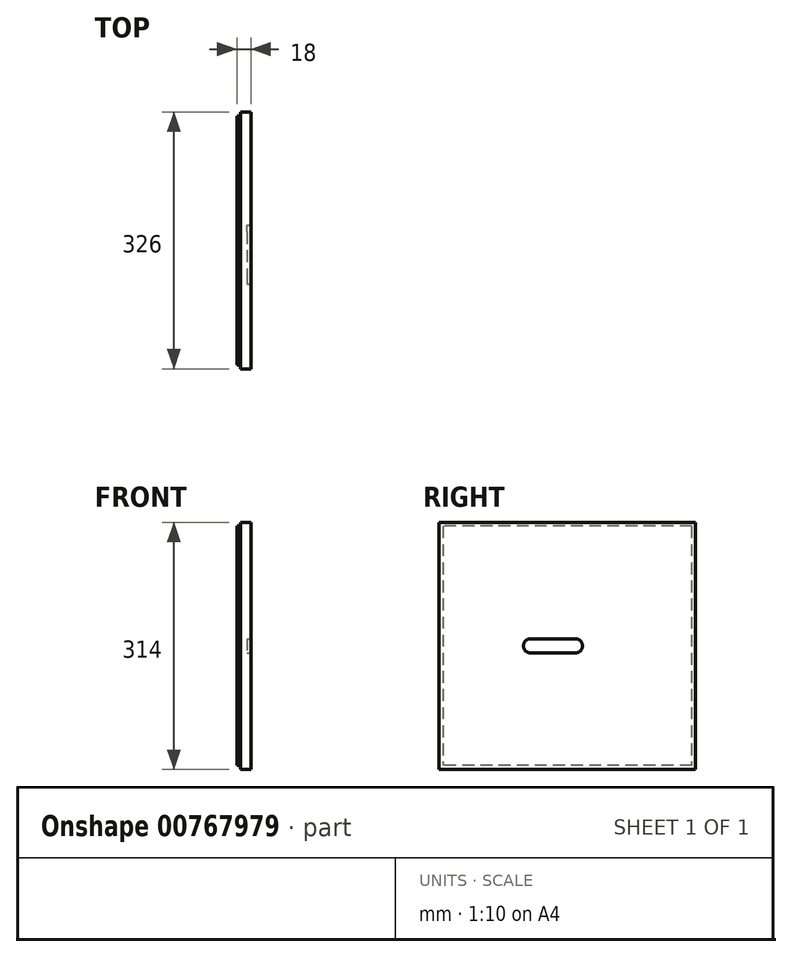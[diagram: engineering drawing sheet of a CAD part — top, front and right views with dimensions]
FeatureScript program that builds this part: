
annotation { "Feature Type Name" : "Feature", "Feature Type Description" : "" }
export const myFeature = defineFeature(function(context is Context, id is Id, definition is map)
    precondition{}
    {
        {
            var Q0;
            Q0=qCreatedBy(makeId("Right.planeOp"),FACE);
            var sketch = newSketch(context, id + "F0", { "sketchPlane" : qUnion([Q0])});
            skLineSegment(sketch, "E0.bottom", {"start": v(-163, 157) * mm, "end": v(163, 157) * mm});
            skLineSegment(sketch, "E0.top", {"start": v(-163, -157) * mm, "end": v(163, -157) * mm});
            skLineSegment(sketch, "E0.left", {"start": v(-163, 157) * mm, "end": v(-163, -157) * mm});
            skLineSegment(sketch, "E0.right", {"start": v(163, 157) * mm, "end": v(163, -157) * mm});
            skPoint(sketch, "E0.middle", {"position": v(0, 0) * mm});
            skSolve(sketch);
        }
        {
            var Q0;
            Q0 = qSketchRegion(id + "F0", true);
            extrude(context, id + "F1", {"entities" : qUnion([Q0]), "oppositeDirection" : true, "depth" : 18 * mm, "offsetDistance" : 25 * mm});
        }
        {
            var Q0;
            Q0=makeQuery(id+"F1.opExtrude","CAP_FACE",FACE,{"disambiguationData":[OSD([sQuery(id+"F0.wireOp",EDGE,"E0.bottom"),sQuery(id+"F0.wireOp",EDGE,"E0.top"),sQuery(id+"F0.wireOp",EDGE,"E0.left"),sQuery(id+"F0.wireOp",EDGE,"E0.right")])],"isStart":true});
            var sketch = newSketch(context, id + "F2", { "sketchPlane" : qUnion([Q0])});
            skLineSegment(sketch, "E1", {"start": v(-163, 0) * mm, "end": v(-18, 0) * mm, "construction": true});
            skLineSegment(sketch, "E2.bottom", {"start": v(10.5, 9) * mm, "end": v(-46.5, 9) * mm});
            skLineSegment(sketch, "E2.top", {"start": v(10.5, -9) * mm, "end": v(-46.5, -9) * mm});
            skLineSegment(sketch, "E2.left", {"start": v(10.5, 9) * mm, "end": v(10.5, -9) * mm, "construction": true});
            skLineSegment(sketch, "E2.right", {"start": v(-46.5, 9) * mm, "end": v(-46.5, -9) * mm, "construction": true});
            skPoint(sketch, "E2.middle", {"position": v(-18, 0) * mm});
            skArc(sketch, "E3", {"start": v(-46.5, 9) * mm, "mid": v(-55.5, 0) * mm, "end": v(-46.5, -9) * mm});
            skArc(sketch, "E4", {"start": v(10.5, 9) * mm, "mid": v(19.5, 0) * mm, "end": v(10.5, -9) * mm});
            skSolve(sketch);
        }
        {
            var Q0;
            Q0 = qSketchRegion(id + "F2", true);
            extrude(context, id + "F3", {"entities" : qUnion([Q0]), "operationType" : NewBodyOperationType.REMOVE, "oppositeDirection" : true, "depth" : 5 * mm, "offsetDistance" : 25 * mm});
        }
        {
            var Q0;
            Q0=makeQuery(id+"F1.opExtrude","CAP_FACE",FACE,{"disambiguationData":[OSD([sQuery(id+"F0.wireOp",EDGE,"E0.bottom"),sQuery(id+"F0.wireOp",EDGE,"E0.top"),sQuery(id+"F0.wireOp",EDGE,"E0.left"),sQuery(id+"F0.wireOp",EDGE,"E0.right")])],"isStart":false});
            var sketch = newSketch(context, id + "F4", { "sketchPlane" : qUnion([Q0])});
            skLineSegment(sketch, "E5.bottom", {"start": v(-163, 157) * mm, "end": v(163, 157) * mm});
            skLineSegment(sketch, "E5.top", {"start": v(-163, -157) * mm, "end": v(163, -157) * mm});
            skLineSegment(sketch, "E5.left", {"start": v(-163, 157) * mm, "end": v(-163, -157) * mm});
            skLineSegment(sketch, "E5.right", {"start": v(163, 157) * mm, "end": v(163, -157) * mm});
            skLineSegment(sketch, "E6.bottom", {"start": v(-158, 152) * mm, "end": v(158, 152) * mm});
            skLineSegment(sketch, "E6.top", {"start": v(-158, -152) * mm, "end": v(158, -152) * mm});
            skLineSegment(sketch, "E6.left", {"start": v(-158, 152) * mm, "end": v(-158, -152) * mm});
            skLineSegment(sketch, "E6.right", {"start": v(158, 152) * mm, "end": v(158, -152) * mm});
            skSolve(sketch);
        }
        {
            var Q0;
            Q0 = qSketchRegion(id + "F4", true);
            extrude(context, id + "F5", {"entities" : qUnion([Q0]), "operationType" : NewBodyOperationType.REMOVE, "oppositeDirection" : true, "depth" : 5 * mm, "offsetDistance" : 25 * mm});
        }
    });
